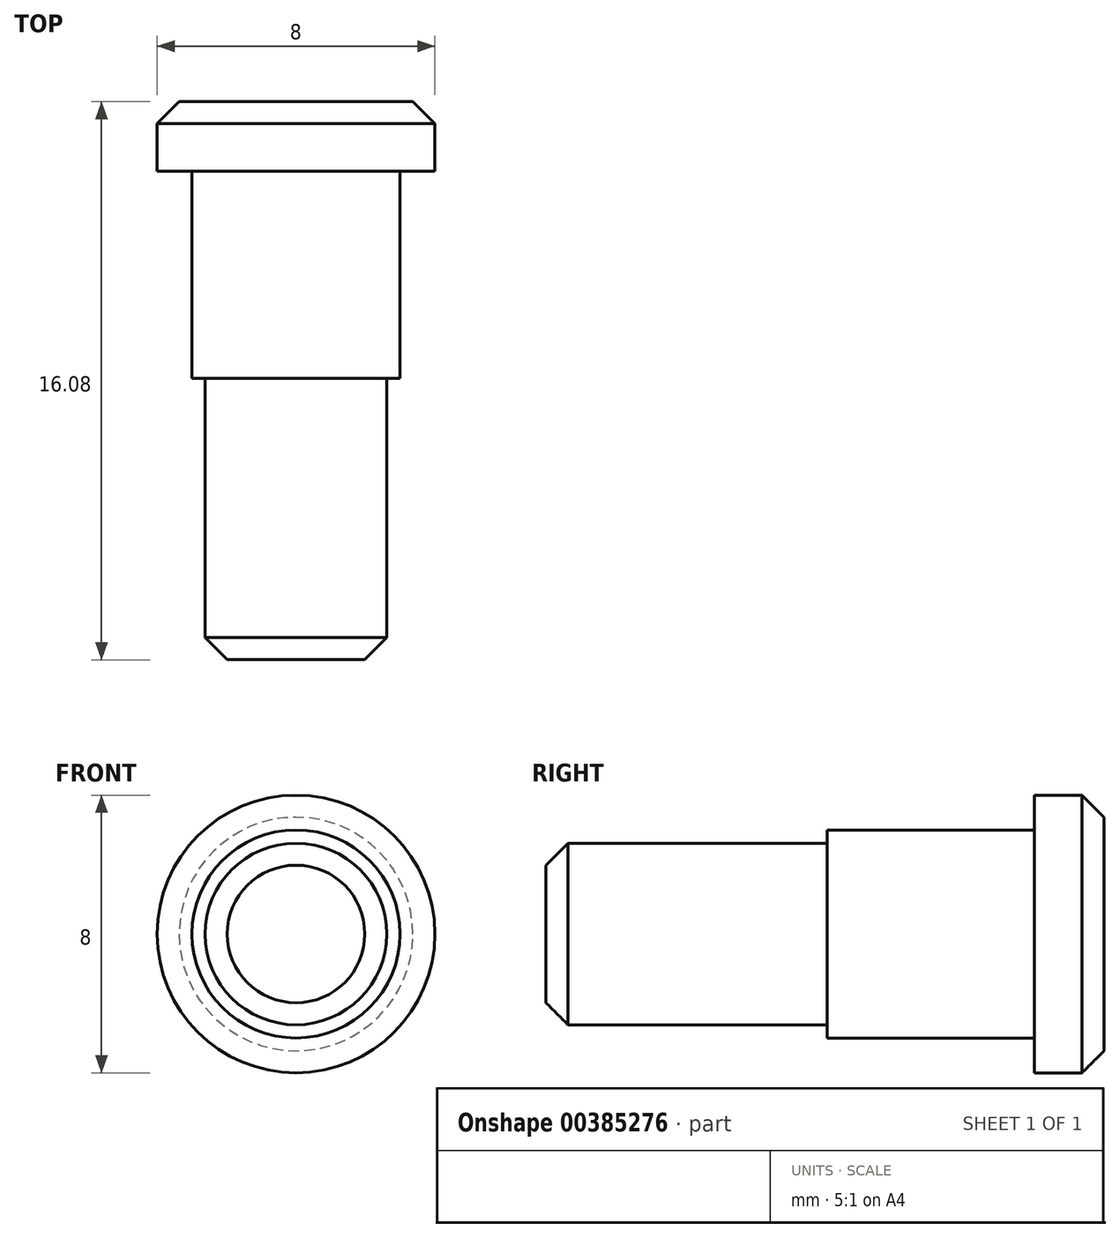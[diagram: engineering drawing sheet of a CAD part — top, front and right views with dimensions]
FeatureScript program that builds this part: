
annotation { "Feature Type Name" : "Feature", "Feature Type Description" : "" }
export const myFeature = defineFeature(function(context is Context, id is Id, definition is map)
    precondition{}
    {
        {
            var Q0;
            Q0=qCreatedBy(makeId("Front.planeOp"),FACE);
            var sketch = newSketch(context, id + "F0", { "sketchPlane" : qUnion([Q0])});
            skCircle(sketch, "E0", {"center": v(0, 0) * mm, "radius": 4 * mm});
            skCircle(sketch, "E1", {"center": v(0, 0) * mm, "radius": 3 * mm});
            skCircle(sketch, "E2", {"center": v(0, 0) * mm, "radius": 2.62 * mm});
            skSolve(sketch);
        }
        {
            var Q0;
            Q0=makeQuery(id+"F0.imprint","IMPRINT",FACE,{"disambiguationData":[TD([[makeQuery(id+"F0.imprint","IMPRINT",EDGE,{"derivedFrom":sQuery(id+"F0.wireOp",EDGE,"E1")}),1.0]])]});
            extrude(context, id + "F1", {"entities" : qUnion([Q0]), "depth" : 7.98 * mm});
        }
        {
            var Q0;
            Q0=makeQuery(id+"F0.imprint","IMPRINT",FACE,{"disambiguationData":[TD([[makeQuery(id+"F0.imprint","IMPRINT",EDGE,{"derivedFrom":sQuery(id+"F0.wireOp",EDGE,"E0")}),1.0]])]});
            extrude(context, id + "F2", {"entities" : qUnion([Q0]), "operationType" : NewBodyOperationType.ADD, "depth" : 2 * mm});
        }
        {
            var Q0;
            Q0=makeQuery(id+"F0.imprint","IMPRINT",FACE,{"disambiguationData":[TD([[makeQuery(id+"F0.imprint","IMPRINT",EDGE,{"derivedFrom":sQuery(id+"F0.wireOp",EDGE,"E2")}),1.0]])]});
            extrude(context, id + "F3", {"entities" : qUnion([Q0]), "operationType" : NewBodyOperationType.ADD, "depth" : 16.08 * mm});
        }
        {
            var Q0;
            Q0=makeQuery(id+"F2.opExtrude","CAP_EDGE",EDGE,{"disambiguationData":[OSD([sQuery(id+"F0.wireOp",EDGE,"E0")])],"isStart":true});
            var Q1;
            Q1=makeQuery(id+"F3.opExtrude","CAP_EDGE",EDGE,{"disambiguationData":[OSD([sQuery(id+"F0.wireOp",EDGE,"E2")])],"isStart":false});
            chamfer(context, id + "F4", {"entities" : qUnion([Q0, Q1]), "width" : 0.64 * mm, "tangentPropagation" : true});
        }
    });
